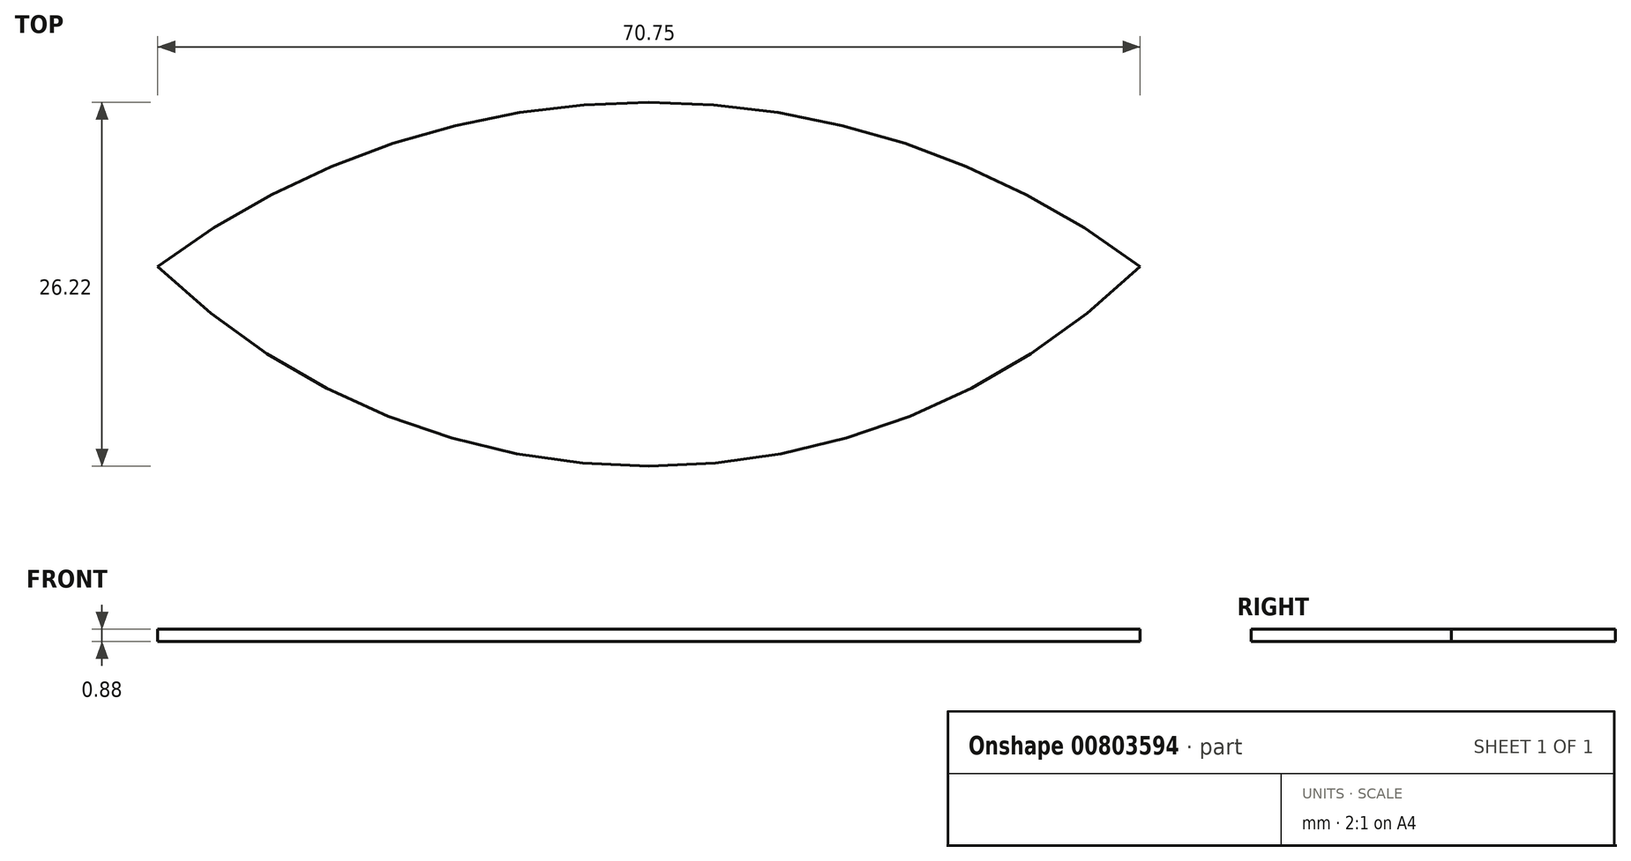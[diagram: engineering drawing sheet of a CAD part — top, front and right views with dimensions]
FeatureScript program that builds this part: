
annotation { "Feature Type Name" : "Feature", "Feature Type Description" : "" }
export const myFeature = defineFeature(function(context is Context, id is Id, definition is map)
    precondition{}
    {
        {
            var Q0;
            Q0=qCreatedBy(makeId("Top.planeOp"),FACE);
            var sketch = newSketch(context, id + "F0", { "sketchPlane" : qUnion([Q0])});
            skLineSegment(sketch, "E0", {"start": v(-35.27, 0) * mm, "end": v(35.48, 0) * mm});
            skArc(sketch, "E1", {"start": v(-35.27, 0) * mm, "mid": v(0.1, -14.4) * mm, "end": v(35.48, 0) * mm});
            skArc(sketch, "E2", {"start": v(35.48, 0) * mm, "mid": v(0.1, 11.83) * mm, "end": v(-35.27, 0) * mm});
            skSolve(sketch);
        }
        {
            var Q0;
            Q0=makeQuery(id+"F0.imprint","IMPRINT",FACE,{"disambiguationData":[TD([[makeQuery(id+"F0.imprint","IMPRINT",EDGE,{"derivedFrom":sQuery(id+"F0.wireOp",EDGE,"E0")}),1.0]])]});
            var Q1;
            Q1=makeQuery(id+"F0.imprint","IMPRINT",FACE,{"disambiguationData":[TD([[makeQuery(id+"F0.imprint","IMPRINT",EDGE,{"derivedFrom":sQuery(id+"F0.wireOp",EDGE,"E0")}),-1.0]])]});
            var Q2;
            Q2=sQuery(id+"F0.wireOp",EDGE,"E1");
            var Q3;
            Q3=sQuery(id+"F0.wireOp",EDGE,"E2");
            extrude(context, id + "F1", {"entities" : qUnion([Q0, Q1]), "bodyType" : ToolBodyType.SURFACE, "surfaceEntities" : qUnion([Q2, Q3]), "depth" : 9 * mm, "offsetDistance" : 25.4 * mm});
        }
        {
            var Q0;
            Q0 = qSketchRegion(id + "F0", true);
            extrude(context, id + "F2", {"entities" : qUnion([Q0]), "depth" : 0.88 * mm, "offsetDistance" : 25.4 * mm});
        }
    });
